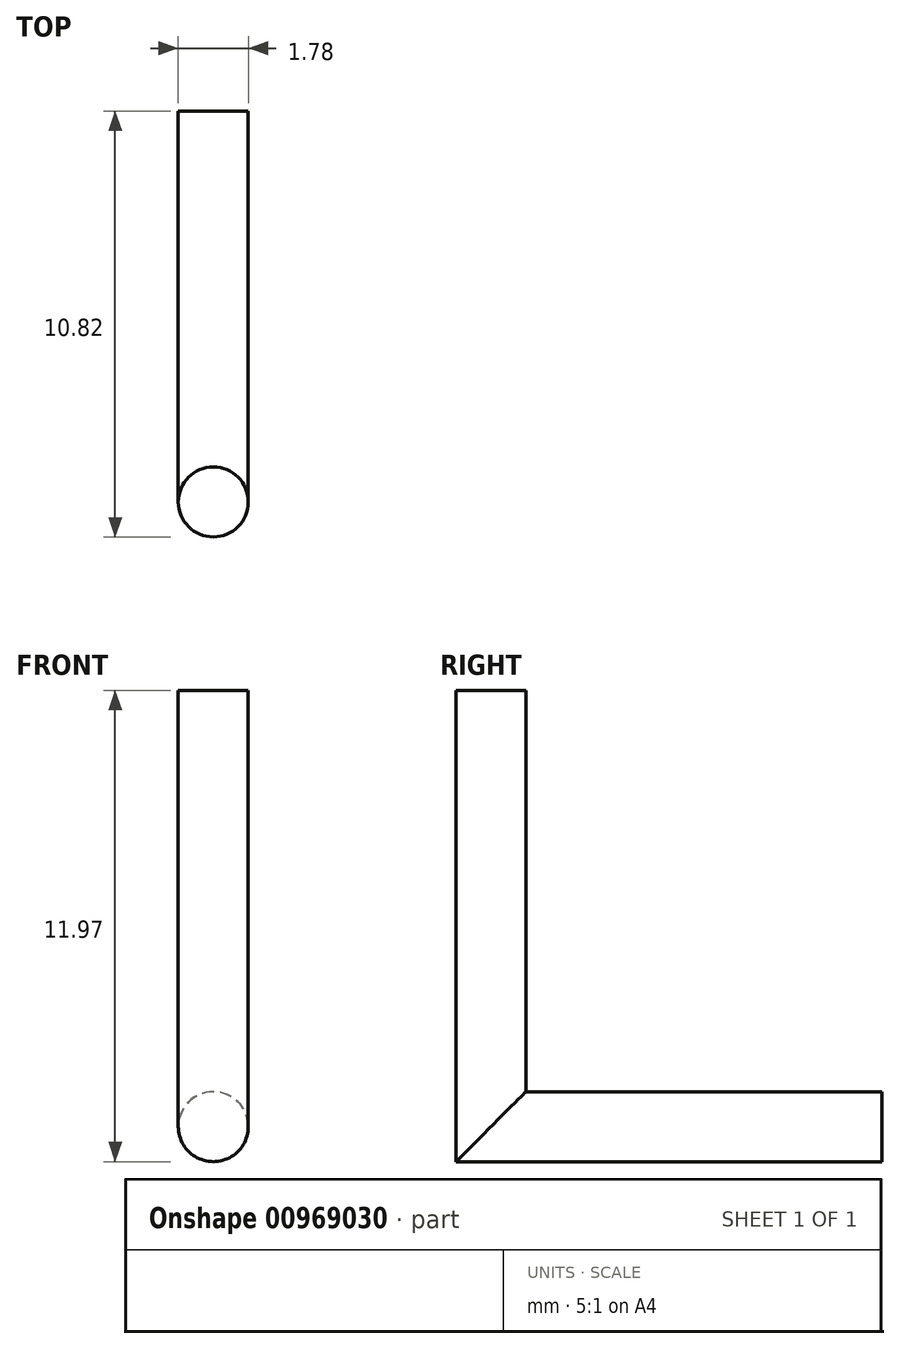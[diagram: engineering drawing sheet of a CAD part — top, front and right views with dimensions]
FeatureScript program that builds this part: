
annotation { "Feature Type Name" : "Feature", "Feature Type Description" : "" }
export const myFeature = defineFeature(function(context is Context, id is Id, definition is map)
    precondition{}
    {
        {
            var Q0;
            Q0=qCreatedBy(makeId("Front.planeOp"),FACE);
            var sketch = newSketch(context, id + "F0", { "sketchPlane" : qUnion([Q0])});
            skCircle(sketch, "E0", {"center": v(0, 0) * mm, "radius": 0.89 * mm});
            skSolve(sketch);
        }
        {
            var Q0;
            Q0=qCreatedBy(makeId("Right.planeOp"),FACE);
            var sketch = newSketch(context, id + "F1", { "sketchPlane" : qUnion([Q0])});
            skLineSegment(sketch, "E1", {"start": v(0, 0) * mm, "end": v(-9.93, 0) * mm});
            skLineSegment(sketch, "E2", {"start": v(-9.93, 0) * mm, "end": v(-9.93, 11.08) * mm});
            skSolve(sketch);
        }
        {
            var Q0;
            Q0=makeQuery(id+"F0.imprint","IMPRINT",FACE,{"disambiguationData":[TD([[makeQuery(id+"F0.imprint","IMPRINT",EDGE,{"derivedFrom":sQuery(id+"F0.wireOp",EDGE,"E0")}),1.0]])]});
            var Q1;
            Q1=sQuery(id+"F1.wireOp",EDGE,"E2");
            var Q2;
            Q2=sQuery(id+"F1.wireOp",EDGE,"E1");
            sweep(context, id + "F2", {"profiles" : qUnion([Q0]), "path" : qUnion([Q1, Q2])});
        }
    });
